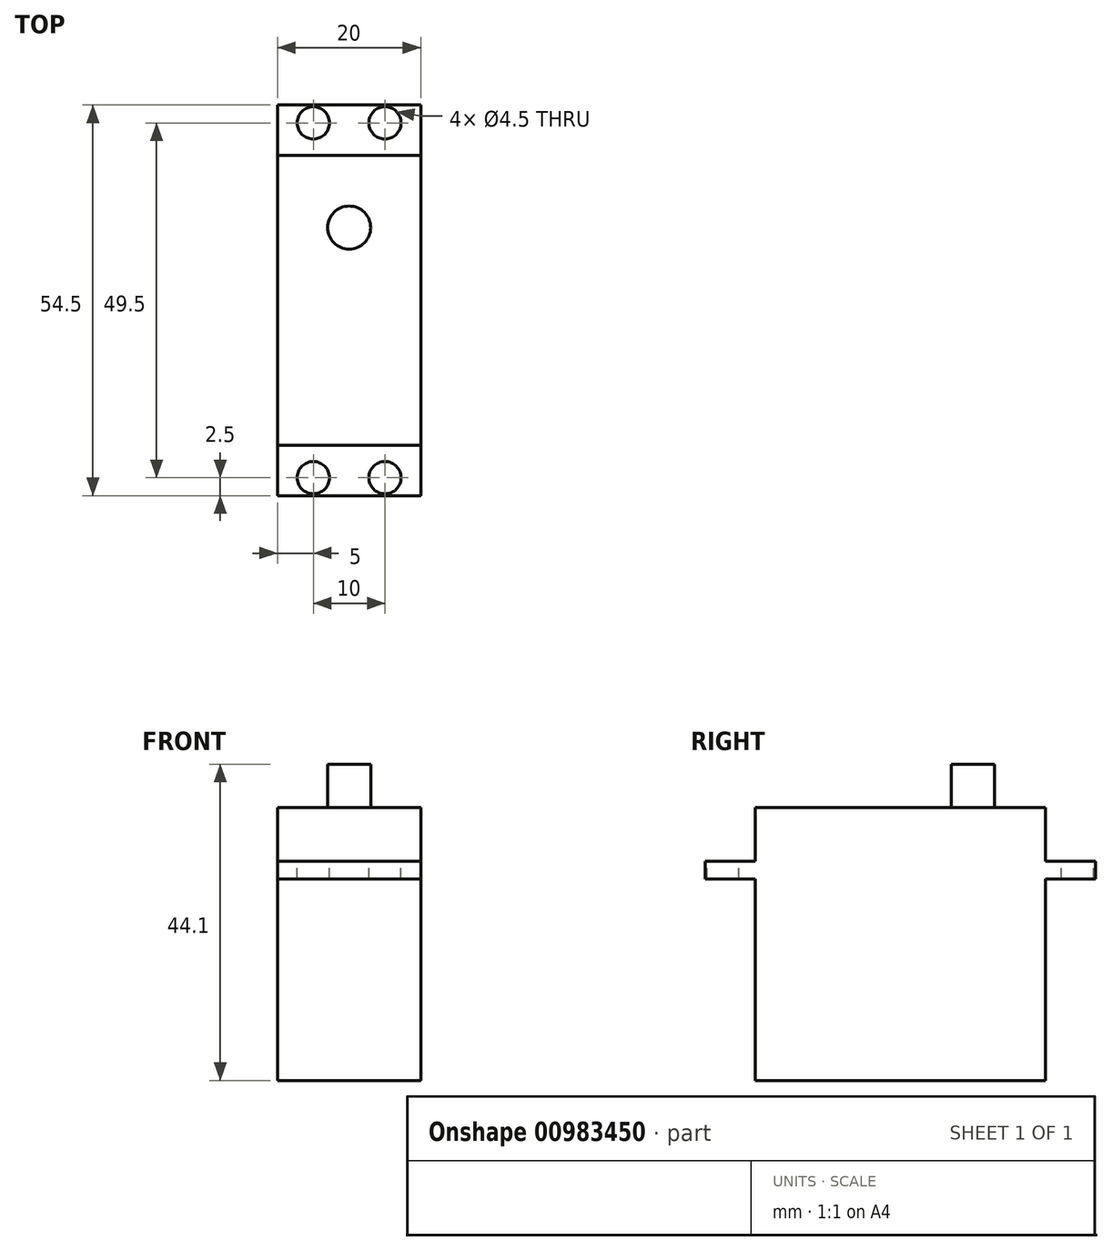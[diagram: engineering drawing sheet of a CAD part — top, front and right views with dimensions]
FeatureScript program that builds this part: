
annotation { "Feature Type Name" : "Feature", "Feature Type Description" : "" }
export const myFeature = defineFeature(function(context is Context, id is Id, definition is map)
    precondition{}
    {
        {
            var Q0;
            Q0=qCreatedBy(makeId("Top.planeOp"),FACE);
            var sketch = newSketch(context, id + "F0", { "sketchPlane" : qUnion([Q0])});
            skLineSegment(sketch, "E0.bottom", {"start": v(10, -20.25) * mm, "end": v(-10, -20.25) * mm});
            skLineSegment(sketch, "E0.top", {"start": v(10, 20.25) * mm, "end": v(-10, 20.25) * mm});
            skLineSegment(sketch, "E0.left", {"start": v(10, -20.25) * mm, "end": v(10, 20.25) * mm});
            skLineSegment(sketch, "E0.right", {"start": v(-10, -20.25) * mm, "end": v(-10, 20.25) * mm});
            skPoint(sketch, "E0.middle", {"position": v(0, 0) * mm});
            skSolve(sketch);
        }
        {
            var Q0;
            Q0=makeQuery(id+"F0.imprint","IMPRINT",FACE,{"disambiguationData":[TD([[makeQuery(id+"F0.imprint","IMPRINT",EDGE,{"derivedFrom":sQuery(id+"F0.wireOp",EDGE,"E0.bottom")}),-1.0]])]});
            extrude(context, id + "F1", {"entities" : qUnion([Q0]), "depth" : 38.1 * mm, "offsetDistance" : 25 * mm});
        }
        {
            var Q0;
            Q0=qCreatedBy(makeId("Top.planeOp"),FACE);
            var sketch = newSketch(context, id + "F2", { "sketchPlane" : qUnion([Q0])});
            skLineSegment(sketch, "E1.bottom", {"start": v(10, -27.25) * mm, "end": v(-10, -27.25) * mm});
            skLineSegment(sketch, "E1.top", {"start": v(10, 27.25) * mm, "end": v(-10, 27.25) * mm});
            skLineSegment(sketch, "E1.left", {"start": v(10, -27.25) * mm, "end": v(10, 27.25) * mm});
            skLineSegment(sketch, "E1.right", {"start": v(-10, -27.25) * mm, "end": v(-10, 27.25) * mm});
            skPoint(sketch, "E1.middle", {"position": v(0, 0) * mm});
            skSolve(sketch);
        }
        {
            var Q0;
            Q0=makeQuery(id+"F2.imprint","IMPRINT",FACE,{"disambiguationData":[TD([[makeQuery(id+"F2.imprint","IMPRINT",EDGE,{"derivedFrom":sQuery(id+"F2.wireOp",EDGE,"E1.bottom")}),-1.0]])]});
            extrude(context, id + "F3", {"entities" : qUnion([Q0]), "operationType" : NewBodyOperationType.ADD, "depth" : 30.6 * mm, "offsetDistance" : 25 * mm, "hasSecondDirection" : true, "secondDirectionOppositeDirection" : false, "secondDirectionDepth" : 28.1 * mm});
        }
        {
            var Q0;
            {var subQ0=sQuery(id+"F2.wireOp",EDGE,"E1.bottom");var subQ1=sQuery(id+"F2.wireOp",EDGE,"E1.left");var subQ2=sQuery(id+"F2.wireOp",EDGE,"E1.right");Q0=makeQuery(id+"F3.boolean.opBoolean","SPLIT",FACE,{"disambiguationData":[TD([makeQuery(id+"F1.opExtrude","SWEPT_FACE",FACE,{"disambiguationData":[OSD([sQuery(id+"F0.wireOp",EDGE,"E0.bottom")])]})])],"derivedFrom":makeQuery(id+"F3.opExtrude","CAP_FACE",FACE,{"disambiguationData":[OSD([subQ0,sQuery(id+"F2.wireOp",EDGE,"E1.top"),subQ1,subQ2])],"isStart":false})});}
            var sketch = newSketch(context, id + "F4", { "sketchPlane" : qUnion([Q0])});
            skCircle(sketch, "E2", {"center": v(-5, -24.75) * mm, "radius": 2.25 * mm});
            skCircle(sketch, "E3", {"center": v(5, -24.75) * mm, "radius": 2.25 * mm});
            skCircle(sketch, "E4", {"center": v(-5, 24.75) * mm, "radius": 2.25 * mm});
            skCircle(sketch, "E5", {"center": v(5, 24.75) * mm, "radius": 2.25 * mm});
            skSolve(sketch);
        }
        {
            var Q0;
            Q0=makeQuery(id+"F4.imprint","IMPRINT",FACE,{"disambiguationData":[TD([[makeQuery(id+"F4.imprint","IMPRINT",EDGE,{"derivedFrom":sQuery(id+"F4.wireOp",EDGE,"E4")}),1.0]])]});
            var Q1;
            Q1=makeQuery(id+"F4.imprint","IMPRINT",FACE,{"disambiguationData":[TD([[makeQuery(id+"F4.imprint","IMPRINT",EDGE,{"derivedFrom":sQuery(id+"F4.wireOp",EDGE,"E5")}),1.0]])]});
            var Q2;
            Q2=makeQuery(id+"F4.imprint","IMPRINT",FACE,{"disambiguationData":[TD([[makeQuery(id+"F4.imprint","IMPRINT",EDGE,{"derivedFrom":sQuery(id+"F4.wireOp",EDGE,"E3")}),1.0]])]});
            var Q3;
            Q3=makeQuery(id+"F4.imprint","IMPRINT",FACE,{"disambiguationData":[TD([[makeQuery(id+"F4.imprint","IMPRINT",EDGE,{"derivedFrom":sQuery(id+"F4.wireOp",EDGE,"E2")}),1.0]])]});
            extrude(context, id + "F5", {"entities" : qUnion([Q0, Q1, Q2, Q3]), "operationType" : NewBodyOperationType.REMOVE, "oppositeDirection" : true, "depth" : 2.5 * mm, "offsetDistance" : 25 * mm});
        }
        {
            var Q0;
            Q0=makeQuery(id+"F1.opExtrude","CAP_FACE",FACE,{"disambiguationData":[OSD([sQuery(id+"F0.wireOp",EDGE,"E0.bottom"),sQuery(id+"F0.wireOp",EDGE,"E0.top"),sQuery(id+"F0.wireOp",EDGE,"E0.left"),sQuery(id+"F0.wireOp",EDGE,"E0.right")])],"isStart":false});
            var sketch = newSketch(context, id + "F6", { "sketchPlane" : qUnion([Q0])});
            skCircle(sketch, "E6", {"center": v(0, 10.15) * mm, "radius": 3 * mm});
            skSolve(sketch);
        }
        {
            var Q0;
            Q0=makeQuery(id+"F6.imprint","IMPRINT",FACE,{"disambiguationData":[TD([[makeQuery(id+"F6.imprint","IMPRINT",EDGE,{"derivedFrom":sQuery(id+"F6.wireOp",EDGE,"E6")}),1.0]])]});
            extrude(context, id + "F7", {"entities" : qUnion([Q0]), "operationType" : NewBodyOperationType.ADD, "depth" : 6 * mm, "offsetDistance" : 25 * mm});
        }
    });
